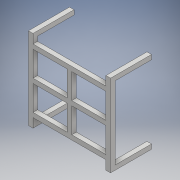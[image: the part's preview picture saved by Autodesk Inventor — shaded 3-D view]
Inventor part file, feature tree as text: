
AUTODESK INVENTOR PART (.ipt)
format: ipt  version: 2018 (Build 220112000, 112)  size: 380,416 bytes
history: native  units: mm
features: extrude x5, sketch x5
ambient origin geometry x8: Origin, YZ Plane, XZ Plane, XY Plane, X Axis, Y Axis, Z Axis, Center Point
bodies: Solid1 (feature_tree)
feature tree (10):
  extrude  "Extrusion1"  Depth=140.0mm
  extrude  "Extrusion2"  Depth=10.0mm
  extrude  "Extrusion3"  Depth=10.0mm
  extrude  "Extrusion4"  Depth=10.0mm
  extrude  "Extrusion7"  Depth=10.0mm
  sketch  "Sketch1"  dims[d0=180.0mm d1=140.0mm]
  sketch  "Sketch2"  dims[d2=10.0mm d3=10.0mm]
  sketch  "Sketch3"  dims[d4=10.0mm d5=10.0mm]
  sketch  "Sketch4"  dims[d6=5.0mm d7=10.0mm]
  sketch  "Sketch7"  dims[d8=5.0mm d9=10.0mm d10=10.0mm d11=0.0mm d12=10.0mm d13=10.0mm d14=10.0mm d15=20.0mm d16=0.0mm d17=10.0mm d18=20.0mm d19=0.0mm d20=10.0mm d21=10.0mm d22=10.0mm d23=80.0mm d24=0.0mm d40=5.0mm d41=5.0mm d42=4.8mm d45=25.0mm d46=0.0mm d47=4.8mm d50=10.0mm d51=4.8mm d52=4.8mm]
